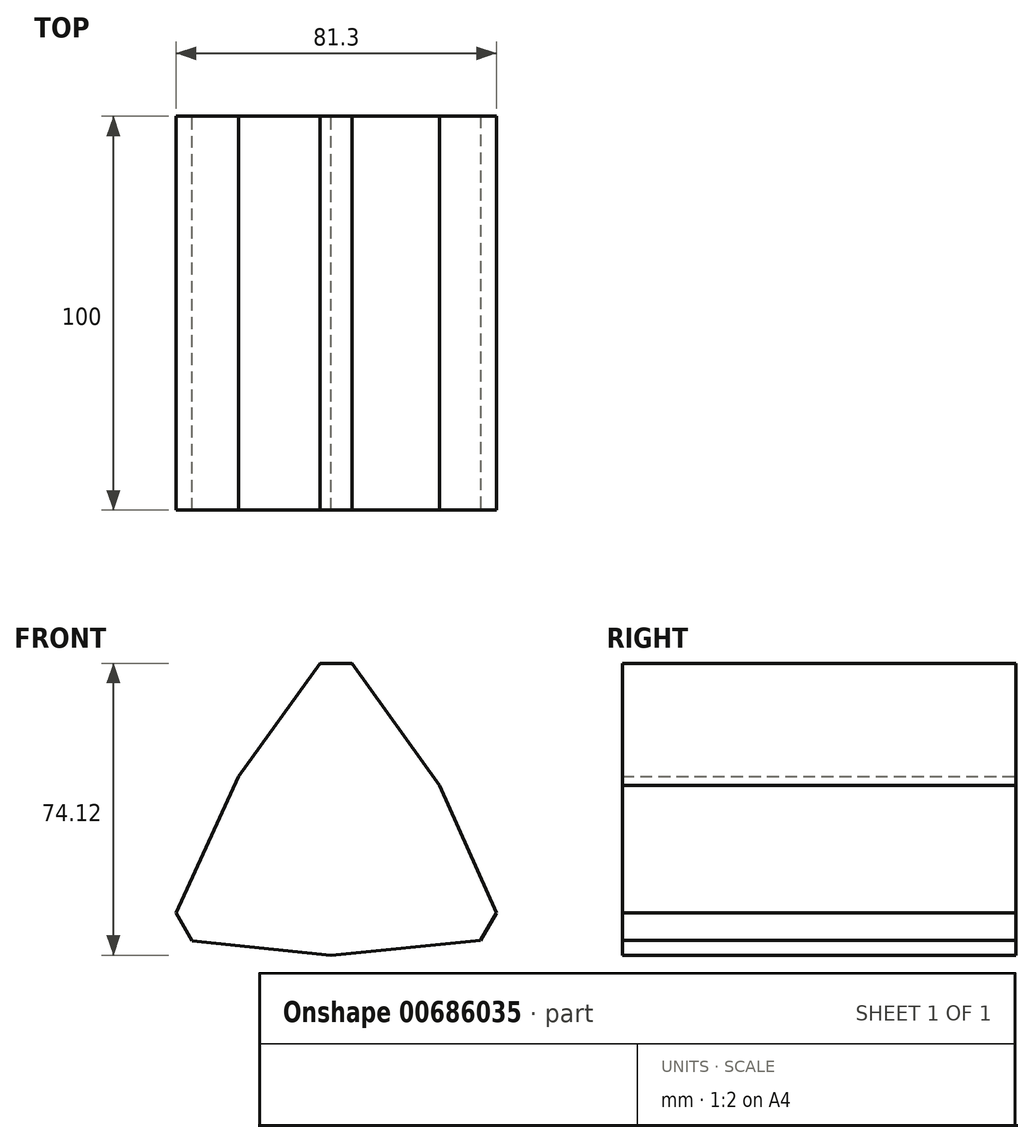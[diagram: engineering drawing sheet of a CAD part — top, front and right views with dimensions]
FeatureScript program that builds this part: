
annotation { "Feature Type Name" : "Feature", "Feature Type Description" : "" }
export const myFeature = defineFeature(function(context is Context, id is Id, definition is map)
    precondition{}
    {
        {
            var Q0;
            Q0=qCreatedBy(makeId("Front.planeOp"),FACE);
            var sketch = newSketch(context, id + "F0", { "sketchPlane" : qUnion([Q0])});
            skLineSegment(sketch, "E0", {"start": v(0, 0) * mm, "end": v(0, 50.23) * mm});
            skLineSegment(sketch, "E1.1.0", {"start": v(0, 0) * mm, "end": v(43.5, -25.11) * mm});
            skLineSegment(sketch, "E1.2.0", {"start": v(0, 0) * mm, "end": v(-43.5, -25.11) * mm});
            skPoint(sketch, "E1.center", {"position": v(0, 0) * mm});
            skLineSegment(sketch, "E1.anchor1", {"start": v(0, 0) * mm, "end": v(0, 50.23) * mm, "construction": true});
            skLineSegment(sketch, "E1.anchor2", {"start": v(0, 0) * mm, "end": v(-43.5, -25.11) * mm, "construction": true});
            skLineSegment(sketch, "E2", {"start": v(0, 0) * mm, "end": v(-24.88, 15.94) * mm});
            skLineSegment(sketch, "E3.1.0", {"start": v(0, 0) * mm, "end": v(-1.37, -29.51) * mm});
            skLineSegment(sketch, "E3.2.0", {"start": v(0, 0) * mm, "end": v(26.25, 13.57) * mm});
            skLineSegment(sketch, "E4", {"start": v(-24.88, 15.94) * mm, "end": v(0, 50.23) * mm});
            skLineSegment(sketch, "E5", {"start": v(0, 50.23) * mm, "end": v(26.25, 13.57) * mm});
            skLineSegment(sketch, "E6", {"start": v(26.25, 13.57) * mm, "end": v(43.5, -25.11) * mm});
            skLineSegment(sketch, "E7", {"start": v(43.5, -25.11) * mm, "end": v(-1.37, -29.51) * mm});
            skLineSegment(sketch, "E8", {"start": v(-1.37, -29.51) * mm, "end": v(-43.5, -25.11) * mm});
            skLineSegment(sketch, "E9", {"start": v(-43.5, -25.11) * mm, "end": v(-24.88, 15.94) * mm});
            skSolve(sketch);
        }
        {
            var Q0;
            Q0=makeQuery(id+"F0.imprint","IMPRINT",FACE,{"disambiguationData":[TD([[makeQuery(id+"F0.imprint","IMPRINT",EDGE,{"derivedFrom":sQuery(id+"F0.wireOp",EDGE,"E1.1.0")}),1.0]])]});
            var Q1;
            Q1=makeQuery(id+"F0.imprint","IMPRINT",FACE,{"disambiguationData":[TD([[makeQuery(id+"F0.imprint","IMPRINT",EDGE,{"derivedFrom":sQuery(id+"F0.wireOp",EDGE,"E1.1.0")}),-1.0]])]});
            var Q2;
            Q2=makeQuery(id+"F0.imprint","IMPRINT",FACE,{"disambiguationData":[TD([[makeQuery(id+"F0.imprint","IMPRINT",EDGE,{"derivedFrom":sQuery(id+"F0.wireOp",EDGE,"E0")}),-1.0]])]});
            var Q3;
            Q3=makeQuery(id+"F0.imprint","IMPRINT",FACE,{"disambiguationData":[TD([[makeQuery(id+"F0.imprint","IMPRINT",EDGE,{"derivedFrom":sQuery(id+"F0.wireOp",EDGE,"E0")}),1.0]])]});
            var Q4;
            Q4=makeQuery(id+"F0.imprint","IMPRINT",FACE,{"disambiguationData":[TD([[makeQuery(id+"F0.imprint","IMPRINT",EDGE,{"derivedFrom":sQuery(id+"F0.wireOp",EDGE,"E1.2.0")}),-1.0]])]});
            var Q5;
            Q5=makeQuery(id+"F0.imprint","IMPRINT",FACE,{"disambiguationData":[TD([[makeQuery(id+"F0.imprint","IMPRINT",EDGE,{"derivedFrom":sQuery(id+"F0.wireOp",EDGE,"E1.2.0")}),1.0]])]});
            extrude(context, id + "F1", {"entities" : qUnion([Q0, Q1, Q2, Q3, Q4, Q5]), "endBound" : BoundingType.SYMMETRIC, "depth" : 100 * mm, "offsetDistance" : 25 * mm});
        }
        {
            var Q0;
            Q0=makeQuery(id+"F1.opExtrude","SWEPT_EDGE",EDGE,{"disambiguationData":[OSD([sQuery(id+"F0.wireOp",EDGE,"E1.2.0"),sQuery(id+"F0.wireOp",EDGE,"E8"),sQuery(id+"F0.wireOp",EDGE,"E9")])]});
            var Q1;
            Q1=makeQuery(id+"F1.opExtrude","SWEPT_EDGE",EDGE,{"disambiguationData":[OSD([sQuery(id+"F0.wireOp",EDGE,"E1.1.0"),sQuery(id+"F0.wireOp",EDGE,"E6"),sQuery(id+"F0.wireOp",EDGE,"E7")])]});
            var Q2;
            Q2=makeQuery(id+"F1.opExtrude","SWEPT_EDGE",EDGE,{"disambiguationData":[OSD([sQuery(id+"F0.wireOp",EDGE,"E0"),sQuery(id+"F0.wireOp",EDGE,"E4"),sQuery(id+"F0.wireOp",EDGE,"E5")])]});
            chamfer(context, id + "F2", {"entities" : qUnion([Q0, Q1, Q2]), "width" : 5 * mm, "tangentPropagation" : true});
        }
    });
